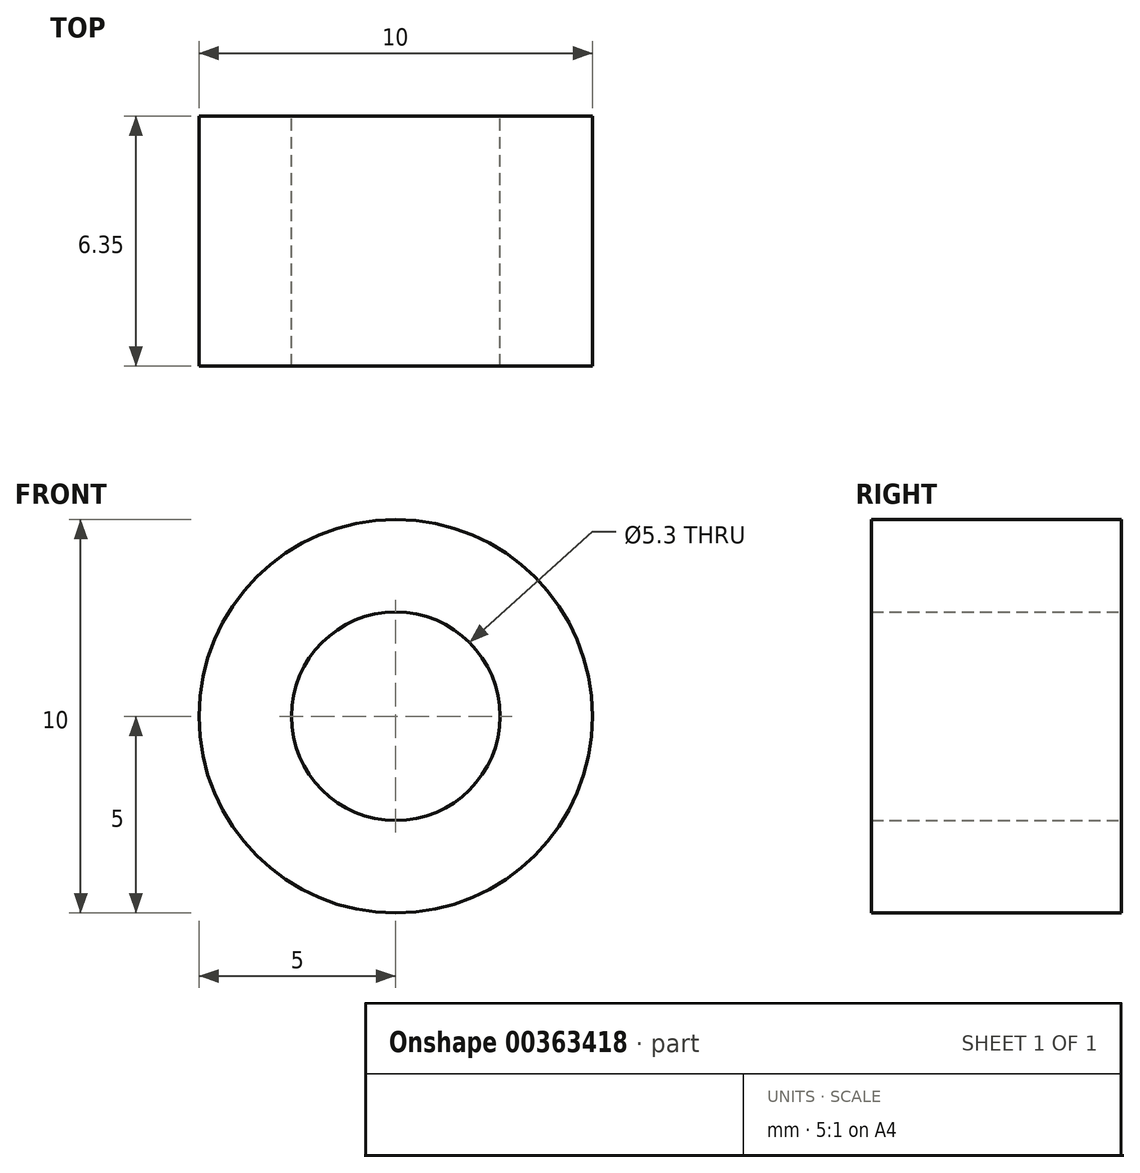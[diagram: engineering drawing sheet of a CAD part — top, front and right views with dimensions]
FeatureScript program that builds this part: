
annotation { "Feature Type Name" : "Feature", "Feature Type Description" : "" }
export const myFeature = defineFeature(function(context is Context, id is Id, definition is map)
    precondition{}
    {
        {
            var Q0;
            Q0=qCreatedBy(makeId("Front.planeOp"),FACE);
            var sketch = newSketch(context, id + "F0", { "sketchPlane" : qUnion([Q0])});
            skCircle(sketch, "E0", {"center": v(0, 0) * mm, "radius": 2.65 * mm});
            skCircle(sketch, "E1", {"center": v(0, 0) * mm, "radius": 5 * mm});
            skSolve(sketch);
        }
        {
            var Q0;
            Q0=makeQuery(id+"F0.imprint","IMPRINT",FACE,{"disambiguationData":[TD([[makeQuery(id+"F0.imprint","IMPRINT",EDGE,{"derivedFrom":sQuery(id+"F0.wireOp",EDGE,"E0")}),-1.0]])]});
            extrude(context, id + "F1", {"entities" : qUnion([Q0]), "depth" : 6.35 * mm, "offsetDistance" : 25 * mm});
        }
    });
